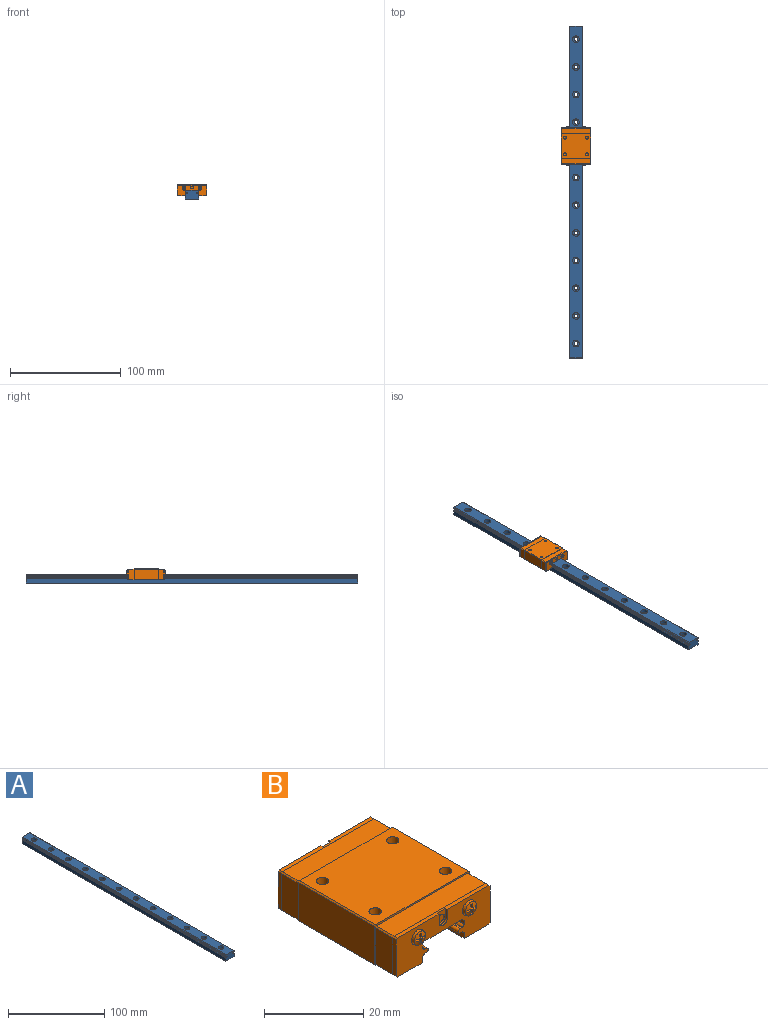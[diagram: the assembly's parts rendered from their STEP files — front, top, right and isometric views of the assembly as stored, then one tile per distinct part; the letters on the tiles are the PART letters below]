
ASSEMBLY  parts=2 mates=1
PART A: 64 faces, bbox 12x300x8 mm
  f0: cylinder r=1.75mm len=5mm, axis (0,0,1), area 55mm2, adj f13,f62
  f1: cylinder r=1.75mm len=5mm, axis (0,0,1), area 55mm2, adj f13,f60
  f2: cylinder r=1.75mm len=5mm, axis (0,0,1), area 55mm2, adj f13,f58
  f3: cylinder r=1.75mm len=5mm, axis (0,0,1), area 55mm2, adj f13,f56
  f4: cylinder r=1.75mm len=5mm, axis (0,0,1), area 55mm2, adj f13,f54
  f5: cylinder r=1.75mm len=5mm, axis (0,0,1), area 55mm2, adj f13,f52
  f6: cylinder r=1.75mm len=5mm, axis (0,0,1), area 55mm2, adj f13,f50
  f7: cylinder r=1.75mm len=5mm, axis (0,0,1), area 55mm2, adj f13,f48
  f8: cylinder r=1.75mm len=5mm, axis (0,0,1), area 55mm2, adj f13,f46
  f9: cylinder r=1.75mm len=5mm, axis (0,0,1), area 55mm2, adj f13,f44
  f10: cylinder r=1.75mm len=5mm, axis (0,0,1), area 55mm2, adj f13,f42
  f11: cylinder r=1.75mm len=5mm, axis (0,0,1), area 55mm2, adj f13,f40
  f12: plane 300x4.32mm, normal (-1,0,0), area 1296.5mm2, adj f13,f28,f29,f39
  f13: plane 300x12mm, normal (0,0,-1), area 3484.5mm2, adj f0,f1,f2,f3,f4,f5,f6,f7
  f14: plane 300x4.32mm, normal (1,0,0), area 1296.5mm2, adj f13,f28,f29,f32
  f15: cylinder r=1.14mm len=300mm, axis (0,1,0), area 187.8mm2, adj f28,f29,f32,f33
  f16: plane 300x0.42mm, normal (0,0,1), area 127.3mm2, adj f17,f28,f29,f33
  f17: cylinder r=0.5mm len=300mm, axis (0,1,0), area 565.5mm2, adj f16,f18,f28,f29
  f18: plane 300x0.42mm, normal (0,0,-1), area 126.3mm2, adj f17,f28,f29,f34
  f19: cylinder r=1.14mm len=300mm, axis (0,1,0), area 188mm2, adj f28,f29,f34,f35
  f20: plane 300x0.91mm, normal (1,0,0), area 272.9mm2, adj f28,f29,f31,f35
  f21: plane 300x11mm, normal (0,0,1), area 2960.7mm2, adj f28,f29,f30,f31,f41,f43,f45,f47
  f22: plane 300x0.91mm, normal (-1,0,0), area 272.9mm2, adj f28,f29,f30,f36
  f23: cylinder r=1.14mm len=300mm, axis (0,1,0), area 188mm2, adj f28,f29,f36,f37
  f24: plane 300x0.42mm, normal (0,0,-1), area 126.3mm2, adj f25,f28,f29,f37
  f25: cylinder r=0.5mm len=300mm, axis (0,1,0), area 565.5mm2, adj f24,f26,f28,f29
  f26: plane 300x0.42mm, normal (0,0,1), area 127.3mm2, adj f25,f28,f29,f38
  f27: cylinder r=1.14mm len=300mm, axis (0,1,0), area 187.8mm2, adj f28,f29,f38,f39
  f28: plane 12x8mm, normal (0,-1,0), area 91.8mm2, adj f12,f13,f14,f15,f16,f17,f18,f19
  f29: plane 12x8mm, normal (0,1,0), area 91.8mm2, adj f12,f13,f14,f15,f16,f17,f18,f19
  f30: plane 300x0.5mm, normal (-0.71,0,0.71), area 212.1mm2, adj f21,f22,f28,f29
  f31: plane 300x0.5mm, normal (0.71,0,0.71), area 212.1mm2, adj f20,f21,f28,f29
  f32: cylinder r=0.16mm len=300mm, axis (0,1,0), area 50.9mm2, adj f14,f15,f28,f29
  f33: cylinder r=0.16mm len=300mm, axis (0,1,0), area 50.9mm2, adj f15,f16,f28,f29
  f34: cylinder r=0.16mm len=300mm, axis (0,1,0), area 50.9mm2, adj f18,f19,f28,f29
  f35: cylinder r=0.16mm len=300mm, axis (0,1,0), area 50.9mm2, adj f19,f20,f28,f29
  f36: cylinder r=0.16mm len=300mm, axis (0,1,0), area 50.9mm2, adj f22,f23,f28,f29
  f37: cylinder r=0.16mm len=300mm, axis (0,1,0), area 50.9mm2, adj f23,f24,f28,f29
  f38: cylinder r=0.16mm len=300mm, axis (0,1,0), area 50.9mm2, adj f26,f27,f28,f29
  f39: cylinder r=0.16mm len=300mm, axis (0,1,0), area 50.9mm2, adj f12,f27,f28,f29
  f40: plane 6x6mm, normal (0,0,1), area 18.7mm2, adj f11,f41
  f41: cylinder r=3mm len=6mm, axis (0,0,1), area 56.5mm2, adj f21,f40
  f42: plane 6x6mm, normal (0,0,1), area 18.7mm2, adj f10,f43
  f43: cylinder r=3mm len=6mm, axis (0,0,1), area 56.5mm2, adj f21,f42
  f44: plane 6x6mm, normal (0,0,1), area 18.7mm2, adj f9,f45
  f45: cylinder r=3mm len=6mm, axis (0,0,1), area 56.5mm2, adj f21,f44
  f46: plane 6x6mm, normal (0,0,1), area 18.7mm2, adj f8,f47
  f47: cylinder r=3mm len=6mm, axis (0,0,1), area 56.5mm2, adj f21,f46
  f48: plane 6x6mm, normal (0,0,1), area 18.7mm2, adj f7,f49
  f49: cylinder r=3mm len=6mm, axis (0,0,1), area 56.5mm2, adj f21,f48
  f50: plane 6x6mm, normal (0,0,1), area 18.7mm2, adj f6,f51
  f51: cylinder r=3mm len=6mm, axis (0,0,1), area 56.5mm2, adj f21,f50
  f52: plane 6x6mm, normal (0,0,1), area 18.7mm2, adj f5,f53
  f53: cylinder r=3mm len=6mm, axis (0,0,1), area 56.5mm2, adj f21,f52
  f54: plane 6x6mm, normal (0,0,1), area 18.7mm2, adj f4,f55
  f55: cylinder r=3mm len=6mm, axis (0,0,1), area 56.5mm2, adj f21,f54
  f56: plane 6x6mm, normal (0,0,1), area 18.7mm2, adj f3,f57
  f57: cylinder r=3mm len=6mm, axis (0,0,1), area 56.5mm2, adj f21,f56
  f58: plane 6x6mm, normal (0,0,1), area 18.7mm2, adj f2,f59
  f59: cylinder r=3mm len=6mm, axis (0,0,1), area 56.5mm2, adj f21,f58
  f60: plane 6x6mm, normal (0,0,1), area 18.7mm2, adj f1,f61
  f61: cylinder r=3mm len=6mm, axis (0,0,1), area 56.5mm2, adj f21,f60
  f62: plane 6x6mm, normal (0,0,1), area 18.7mm2, adj f0,f63
  f63: cylinder r=3mm len=6mm, axis (0,0,1), area 56.5mm2, adj f21,f62
PART B: 172 faces, bbox 27x35.9x10 mm
  f0: cylinder r=1.25mm len=3.5mm, axis (0,0,-1), area 27.5mm2, adj f1,f158
  f1: cone r=0.62mm half-angle=59deg, axis (0,0,1), area 5.7mm2, adj f0
  f2: cylinder r=1.25mm len=3.5mm, axis (0,0,-1), area 27.5mm2, adj f3,f158
  f3: cone r=0.62mm half-angle=59deg, axis (0,0,1), area 5.7mm2, adj f2
  f4: cylinder r=1.25mm len=3.5mm, axis (0,0,-1), area 27.5mm2, adj f5,f158
  f5: cone r=0.62mm half-angle=59deg, axis (0,0,1), area 5.7mm2, adj f4
  f6: cylinder r=1.25mm len=3.5mm, axis (0,0,-1), area 27.5mm2, adj f7,f158
  f7: cone r=0.62mm half-angle=59deg, axis (0,0,1), area 5.7mm2, adj f6
  f8: cylinder r=0.5mm len=33.7mm, axis (0,1,0), area 63.6mm2, adj f58,f115,f148,f149
  f9: cylinder r=0.5mm len=33.7mm, axis (0,1,0), area 63.6mm2, adj f58,f115,f137,f138
  f10: cylinder r=1.15mm len=2.3mm, axis (0,1,0), area 3.6mm2, adj f114,f124
  f11: cylinder r=1.75mm len=3.5mm, axis (0,1,0), area 5.5mm2, adj f109,f115
  f12: cylinder r=1.75mm len=3.5mm, axis (0,1,0), area 5.5mm2, adj f108,f115
  f13: cone r=0.85mm half-angle=5deg, axis (0,1,0), area 11.5mm2, adj f14,f109
  f14: cone r=0.8mm half-angle=72.7deg, axis (0,1,0), area 6.3mm2, adj f13,f96,f97,f98,f99,f100,f101,f102
  f15: cone r=0.85mm half-angle=5deg, axis (0,1,0), area 11.5mm2, adj f16,f108
  f16: cone r=0.8mm half-angle=72.7deg, axis (0,1,0), area 6.3mm2, adj f15,f83,f84,f85,f86,f87,f88,f89
  f17: cylinder r=1.15mm len=2.3mm, axis (0,-1,0), area 3.6mm2, adj f57,f67
  f18: cylinder r=1.75mm len=3.5mm, axis (0,-1,0), area 5.5mm2, adj f52,f58
  f19: cylinder r=1.75mm len=3.5mm, axis (0,-1,0), area 5.5mm2, adj f51,f58
  f20: cone r=0.85mm half-angle=5deg, axis (0,-1,0), area 11.5mm2, adj f21,f52
  f21: cone r=0.8mm half-angle=72.7deg, axis (0,-1,0), area 6.3mm2, adj f20,f39,f40,f41,f42,f43,f44,f45
  f22: cone r=0.85mm half-angle=5deg, axis (0,-1,0), area 11.5mm2, adj f23,f51
  f23: cone r=0.8mm half-angle=72.7deg, axis (0,-1,0), area 6.3mm2, adj f22,f26,f27,f28,f29,f30,f31,f32
  f24: plane 26.6x9.6mm, normal (0,-1,0), area 0.3mm2, adj f55,f59,f60,f61,f62,f63,f64,f65
  f25: plane 2.4x2.4mm, normal (0,1,0), area 2.1mm2, adj f26,f27,f28,f29,f30,f31,f32,f33
  f26: plane 0.93x0.49mm, normal (0,0,1), area 0.4mm2, adj f23,f25,f29,f31
  f27: plane 0.93x0.49mm, normal (0,0,-1), area 0.4mm2, adj f23,f25,f28,f30
  f28: plane 1.36x1.29mm, normal (-1,0,0), area 1mm2, adj f23,f25,f27,f36
  f29: plane 1.36x1.29mm, normal (-1,0,0), area 1mm2, adj f23,f25,f26,f32
  f30: plane 1.36x1.29mm, normal (1,0,0), area 1mm2, adj f23,f25,f27,f33
  f31: plane 1.36x1.29mm, normal (1,0,0), area 1mm2, adj f23,f25,f26,f34
  f32: plane 1.36x1.29mm, normal (0,0,1), area 1mm2, adj f23,f25,f29,f35
  f33: plane 1.36x1.29mm, normal (0,0,-1), area 1mm2, adj f23,f25,f30,f37
  f34: plane 1.36x1.29mm, normal (0,0,1), area 1mm2, adj f23,f25,f31,f37
  f35: plane 0.93x0.49mm, normal (-1,0,0), area 0.4mm2, adj f23,f25,f32,f36
  f36: plane 1.36x1.29mm, normal (0,0,-1), area 1mm2, adj f23,f25,f28,f35
  f37: plane 0.94x0.49mm, normal (1,0,0), area 0.4mm2, adj f23,f25,f33,f34
  f38: plane 2.4x2.4mm, normal (0,1,0), area 2.1mm2, adj f39,f40,f41,f42,f43,f44,f45,f46
  f39: plane 0.93x0.49mm, normal (0,0,1), area 0.4mm2, adj f21,f38,f42,f44
  f40: plane 0.93x0.49mm, normal (0,0,-1), area 0.4mm2, adj f21,f38,f41,f43
  f41: plane 1.36x1.29mm, normal (-1,0,0), area 1mm2, adj f21,f38,f40,f49
  f42: plane 1.36x1.29mm, normal (-1,0,0), area 1mm2, adj f21,f38,f39,f45
  f43: plane 1.36x1.29mm, normal (1,0,0), area 1mm2, adj f21,f38,f40,f46
  f44: plane 1.36x1.29mm, normal (1,0,0), area 1mm2, adj f21,f38,f39,f47
  f45: plane 1.36x1.29mm, normal (0,0,1), area 1mm2, adj f21,f38,f42,f48
  f46: plane 1.36x1.29mm, normal (0,0,-1), area 1mm2, adj f21,f38,f43,f50
  f47: plane 1.36x1.29mm, normal (0,0,1), area 1mm2, adj f21,f38,f44,f50
  f48: plane 0.93x0.49mm, normal (-1,0,0), area 0.4mm2, adj f21,f38,f45,f49
  f49: plane 1.36x1.29mm, normal (0,0,-1), area 1mm2, adj f21,f38,f41,f48
  f50: plane 0.94x0.49mm, normal (1,0,0), area 0.4mm2, adj f21,f38,f46,f47
  f51: plane 3.5x3.5mm, normal (0,1,0), area 0.5mm2, adj f19,f22
  f52: plane 3.5x3.5mm, normal (0,1,0), area 0.5mm2, adj f18,f20
  f53: plane 2.1x0.5mm, normal (1,0,0), area 1.1mm2, adj f55,f56,f57,f58
  f54: plane 2.1x0.5mm, normal (-1,0,0), area 1.1mm2, adj f55,f56,f57,f58
  f55: plane 26x1mm, normal (0,0,1), area 24.8mm2, adj f24,f53,f54,f57,f58,f62,f63
  f56: cylinder r=1.2mm len=2.4mm, axis (0,-1,0), area 1.9mm2, adj f53,f54,f57,f58
  f57: plane 3.3x2.4mm, normal (0,1,0), area 3.1mm2, adj f17,f53,f54,f55,f56
  f58: plane 26.6x9.6mm, normal (0,1,0), area 172.9mm2, adj f8,f9,f18,f19,f53,f54,f55,f56
  f59: plane 7x1mm, normal (0,0,-1), area 7mm2, adj f24,f58,f65,f134
  f60: plane 7x1mm, normal (0,0,-1), area 7mm2, adj f24,f58,f66,f152
  f61: plane 9x1mm, normal (1,0,0), area 9mm2, adj f24,f58,f62,f66
  f62: plane 1x0.3mm, normal (0.71,0,0.71), area 0.4mm2, adj f24,f55,f58,f61
  f63: plane 1x0.3mm, normal (-0.71,0,0.71), area 0.4mm2, adj f24,f55,f58,f64
  f64: plane 9x1mm, normal (-1,0,0), area 9mm2, adj f24,f58,f63,f65
  f65: plane 1x0.3mm, normal (-0.71,0,-0.71), area 0.4mm2, adj f24,f58,f59,f64
  f66: plane 1x0.3mm, normal (0.71,0,-0.71), area 0.4mm2, adj f24,f58,f60,f61
  f67: plane 2.3x2.3mm, normal (0,1,0), area 4.2mm2, adj f17
  f68: cylinder r=1.14mm len=33.7mm, axis (0,-1,0), area 21.1mm2, adj f58,f115,f150,f151
  f69: cylinder r=1.14mm len=33.7mm, axis (0,-1,0), area 21.1mm2, adj f58,f115,f146,f147
  f70: cylinder r=1.14mm len=33.7mm, axis (0,-1,0), area 21.1mm2, adj f58,f115,f139,f140
  f71: cylinder r=1.14mm len=33.7mm, axis (0,-1,0), area 21.1mm2, adj f58,f115,f135,f136
  f72: plane 7x5mm, normal (0,0,-1), area 35mm2, adj f24,f79,f134,f163
  f73: plane 7x5mm, normal (0,0,-1), area 35mm2, adj f24,f80,f152,f163
  f74: plane 8.99x5mm, normal (1,0,0), area 45mm2, adj f24,f75,f80,f163
  f75: plane 5x0.3mm, normal (0.71,0,0.71), area 2.1mm2, adj f24,f74,f76,f163
  f76: plane 25.99x5mm, normal (0,0,1), area 130mm2, adj f24,f75,f77,f163
  f77: plane 5x0.3mm, normal (-0.71,0,0.71), area 2.1mm2, adj f24,f76,f78,f163
  f78: plane 8.99x5mm, normal (-1,0,0), area 45mm2, adj f24,f77,f79,f163
  f79: plane 5x0.3mm, normal (-0.71,0,-0.71), area 2.1mm2, adj f24,f72,f78,f163
  f80: plane 5x0.3mm, normal (0.71,0,-0.71), area 2.1mm2, adj f24,f73,f74,f163
  f81: plane 26.6x9.6mm, normal (0,1,0), area 0.3mm2, adj f112,f116,f117,f118,f119,f120,f121,f122
  f82: plane 2.4x2.4mm, normal (0,-1,0), area 2.1mm2, adj f83,f84,f85,f86,f87,f88,f89,f90
  f83: plane 0.93x0.49mm, normal (0,0,1), area 0.4mm2, adj f16,f82,f86,f88
  f84: plane 0.93x0.49mm, normal (0,0,-1), area 0.4mm2, adj f16,f82,f85,f87
  f85: plane 1.36x1.29mm, normal (1,0,0), area 1mm2, adj f16,f82,f84,f93
  f86: plane 1.36x1.29mm, normal (1,0,0), area 1mm2, adj f16,f82,f83,f89
  f87: plane 1.36x1.29mm, normal (-1,0,0), area 1mm2, adj f16,f82,f84,f90
  f88: plane 1.36x1.29mm, normal (-1,0,0), area 1mm2, adj f16,f82,f83,f91
  f89: plane 1.36x1.29mm, normal (0,0,1), area 1mm2, adj f16,f82,f86,f92
  f90: plane 1.36x1.29mm, normal (0,0,-1), area 1mm2, adj f16,f82,f87,f94
  f91: plane 1.36x1.29mm, normal (0,0,1), area 1mm2, adj f16,f82,f88,f94
  f92: plane 0.93x0.49mm, normal (1,0,0), area 0.4mm2, adj f16,f82,f89,f93
  f93: plane 1.36x1.29mm, normal (0,0,-1), area 1mm2, adj f16,f82,f85,f92
  f94: plane 0.94x0.49mm, normal (-1,0,0), area 0.4mm2, adj f16,f82,f90,f91
  f95: plane 2.4x2.4mm, normal (0,-1,0), area 2.1mm2, adj f96,f97,f98,f99,f100,f101,f102,f103
  f96: plane 0.93x0.49mm, normal (0,0,1), area 0.4mm2, adj f14,f95,f99,f101
  f97: plane 0.93x0.49mm, normal (0,0,-1), area 0.4mm2, adj f14,f95,f98,f100
  f98: plane 1.36x1.29mm, normal (1,0,0), area 1mm2, adj f14,f95,f97,f106
  f99: plane 1.36x1.29mm, normal (1,0,0), area 1mm2, adj f14,f95,f96,f102
  f100: plane 1.36x1.29mm, normal (-1,0,0), area 1mm2, adj f14,f95,f97,f103
  f101: plane 1.36x1.29mm, normal (-1,0,0), area 1mm2, adj f14,f95,f96,f104
  f102: plane 1.36x1.29mm, normal (0,0,1), area 1mm2, adj f14,f95,f99,f105
  f103: plane 1.36x1.29mm, normal (0,0,-1), area 1mm2, adj f14,f95,f100,f107
  f104: plane 1.36x1.29mm, normal (0,0,1), area 1mm2, adj f14,f95,f101,f107
  f105: plane 0.93x0.49mm, normal (1,0,0), area 0.4mm2, adj f14,f95,f102,f106
  f106: plane 1.36x1.29mm, normal (0,0,-1), area 1mm2, adj f14,f95,f98,f105
  f107: plane 0.94x0.49mm, normal (-1,0,0), area 0.4mm2, adj f14,f95,f103,f104
  f108: plane 3.5x3.5mm, normal (0,-1,0), area 0.5mm2, adj f12,f15
  f109: plane 3.5x3.5mm, normal (0,-1,0), area 0.5mm2, adj f11,f13
  f110: plane 2.1x0.5mm, normal (-1,0,0), area 1mm2, adj f112,f113,f114,f115
  f111: plane 2.1x0.5mm, normal (1,0,0), area 1mm2, adj f112,f113,f114,f115
  f112: plane 26x1mm, normal (0,0,1), area 24.8mm2, adj f81,f110,f111,f114,f115,f119,f120
  f113: cylinder r=1.2mm len=2.4mm, axis (0,1,0), area 1.9mm2, adj f110,f111,f114,f115
  f114: plane 3.3x2.4mm, normal (0,-1,0), area 3.1mm2, adj f10,f110,f111,f112,f113
  f115: plane 26.6x9.6mm, normal (0,-1,0), area 172.9mm2, adj f8,f9,f11,f12,f68,f69,f70,f71
  f116: plane 7x1mm, normal (0,0,-1), area 7mm2, adj f81,f115,f122,f152
  f117: plane 7x1mm, normal (0,0,-1), area 7mm2, adj f81,f115,f123,f134
  f118: plane 9x1mm, normal (-1,0,0), area 9mm2, adj f81,f115,f119,f123
  f119: plane 1x0.3mm, normal (-0.71,0,0.71), area 0.4mm2, adj f81,f112,f115,f118
  f120: plane 1x0.3mm, normal (0.71,0,0.71), area 0.4mm2, adj f81,f112,f115,f121
  f121: plane 9x1mm, normal (1,0,0), area 9mm2, adj f81,f115,f120,f122
  f122: plane 1x0.3mm, normal (0.71,0,-0.71), area 0.4mm2, adj f81,f115,f116,f121
  f123: plane 1x0.3mm, normal (-0.71,0,-0.71), area 0.4mm2, adj f81,f115,f117,f118
  f124: plane 2.3x2.3mm, normal (0,-1,0), area 4.2mm2, adj f10
  f125: plane 7x5mm, normal (0,0,-1), area 35mm2, adj f81,f132,f152,f153
  f126: plane 7x5mm, normal (0,0,-1), area 35mm2, adj f81,f133,f134,f153
  f127: plane 8.99x5mm, normal (-1,0,0), area 44.9mm2, adj f81,f128,f133,f153
  f128: plane 5x0.3mm, normal (-0.71,0,0.71), area 2.1mm2, adj f81,f127,f129,f153
  f129: plane 25.99x5mm, normal (0,0,1), area 129.9mm2, adj f81,f128,f130,f153
  f130: plane 5x0.3mm, normal (0.71,0,0.71), area 2.1mm2, adj f81,f129,f131,f153
  f131: plane 8.99x5mm, normal (1,0,0), area 45mm2, adj f81,f130,f132,f153
  f132: plane 5x0.3mm, normal (0.71,0,-0.71), area 2.1mm2, adj f81,f125,f131,f153
  f133: plane 5x0.3mm, normal (-0.71,0,-0.71), area 2.1mm2, adj f81,f126,f127,f153
  f134: plane 33.7x1.32mm, normal (1,0,0), area 44.5mm2, adj f24,f58,f59,f72,f81,f115,f117,f126
  f135: cylinder r=0.16mm len=33.7mm, axis (0,1,0), area 5.7mm2, adj f58,f71,f115,f134
  f136: cylinder r=0.16mm len=33.7mm, axis (0,1,0), area 5.7mm2, adj f58,f71,f115,f137
  f137: plane 33.7x0.42mm, normal (0,0,-1), area 14.2mm2, adj f9,f58,f115,f136
  f138: plane 33.7x0.42mm, normal (0,0,1), area 14.2mm2, adj f9,f58,f115,f139
  f139: cylinder r=0.16mm len=33.7mm, axis (0,1,0), area 5.7mm2, adj f58,f70,f115,f138
  f140: cylinder r=0.16mm len=33.7mm, axis (0,1,0), area 5.7mm2, adj f58,f70,f115,f141
  f141: plane 33.7x0.82mm, normal (1,0,0), area 27.7mm2, adj f58,f115,f140,f142
  f142: plane 33.7x0.59mm, normal (0.76,0,-0.65), area 26mm2, adj f58,f115,f141,f143
  f143: plane 33.7x11mm, normal (0,0,-1), area 370.7mm2, adj f58,f115,f142,f144
  f144: plane 33.7x0.59mm, normal (-0.76,0,-0.65), area 26mm2, adj f58,f115,f143,f145
  f145: plane 33.7x0.82mm, normal (-1,0,0), area 27.7mm2, adj f58,f115,f144,f146
  f146: cylinder r=0.16mm len=33.7mm, axis (0,1,0), area 5.7mm2, adj f58,f69,f115,f145
  f147: cylinder r=0.16mm len=33.7mm, axis (0,1,0), area 5.7mm2, adj f58,f69,f115,f148
  f148: plane 33.7x0.42mm, normal (0,0,1), area 14.2mm2, adj f8,f58,f115,f147
  f149: plane 33.7x0.42mm, normal (0,0,-1), area 14.2mm2, adj f8,f58,f115,f150
  f150: cylinder r=0.16mm len=33.7mm, axis (0,1,0), area 5.7mm2, adj f58,f68,f115,f149
  f151: cylinder r=0.16mm len=33.7mm, axis (0,1,0), area 5.7mm2, adj f58,f68,f115,f152
  f152: plane 33.7x1.32mm, normal (-1,0,0), area 44.5mm2, adj f24,f58,f60,f73,f81,f115,f116,f125
  f153: plane 27x10mm, normal (0,-1,0), area 14.9mm2, adj f125,f126,f127,f128,f129,f130,f131,f132
  f154: plane 21.7x7.2mm, normal (0,0,-1), area 156.2mm2, adj f152,f153,f161,f163
  f155: plane 21.7x7.2mm, normal (0,0,-1), area 156.2mm2, adj f134,f153,f162,f163
  f156: plane 21.7x9.4mm, normal (-1,0,0), area 204mm2, adj f153,f157,f162,f163
  f157: plane 21.7x0.3mm, normal (-0.71,0,0.71), area 9.2mm2, adj f153,f156,f158,f163
  f158: plane 26.4x21.7mm, normal (0,0,1), area 553.2mm2, adj f0,f2,f4,f6,f153,f157,f159,f163
  f159: plane 21.7x0.3mm, normal (0.71,0,0.71), area 9.2mm2, adj f153,f158,f160,f163
  f160: plane 21.7x9.4mm, normal (1,0,0), area 204mm2, adj f153,f159,f161,f163
  f161: plane 21.7x0.3mm, normal (0.71,0,-0.71), area 9.2mm2, adj f153,f154,f160,f163
  f162: plane 21.7x0.3mm, normal (-0.71,0,-0.71), area 9.2mm2, adj f153,f155,f156,f163
  f163: plane 27x10mm, normal (0,1,0), area 14.9mm2, adj f72,f73,f74,f75,f76,f77,f78,f79
  f164: cone r=0.5mm half-angle=17.1deg, axis (0,-1,0), area 2.7mm2, adj f166,f167
  f165: cylinder r=1.25mm len=2.5mm, axis (0,-1,0), area 3.9mm2, adj f166,f167
  f166: plane 2.5x2.5mm, normal (0,1,0), area 2.3mm2, adj f164,f165
  f167: plane 2.5x2.5mm, normal (0,-1,0), area 3.1mm2, adj f164,f165
  f168: cylinder r=1.25mm len=2.5mm, axis (0,-1,0), area 3.9mm2, adj f170,f171
  f169: cone r=0.5mm half-angle=17.1deg, axis (0,-1,0), area 2.7mm2, adj f170,f171
  f170: plane 2.5x2.5mm, normal (0,-1,0), area 3.1mm2, adj f168,f169
  f171: plane 2.5x2.5mm, normal (0,1,0), area 2.3mm2, adj f168,f169
PLACE A t=(-278.25,496.42,146.89)mm
PLACE B t=(-284.25,371.06,146.89)mm
MATE slider A.f17 <-> B.f8  axis (0,-1,0) through (-279.49,196.42,152.35)mm
